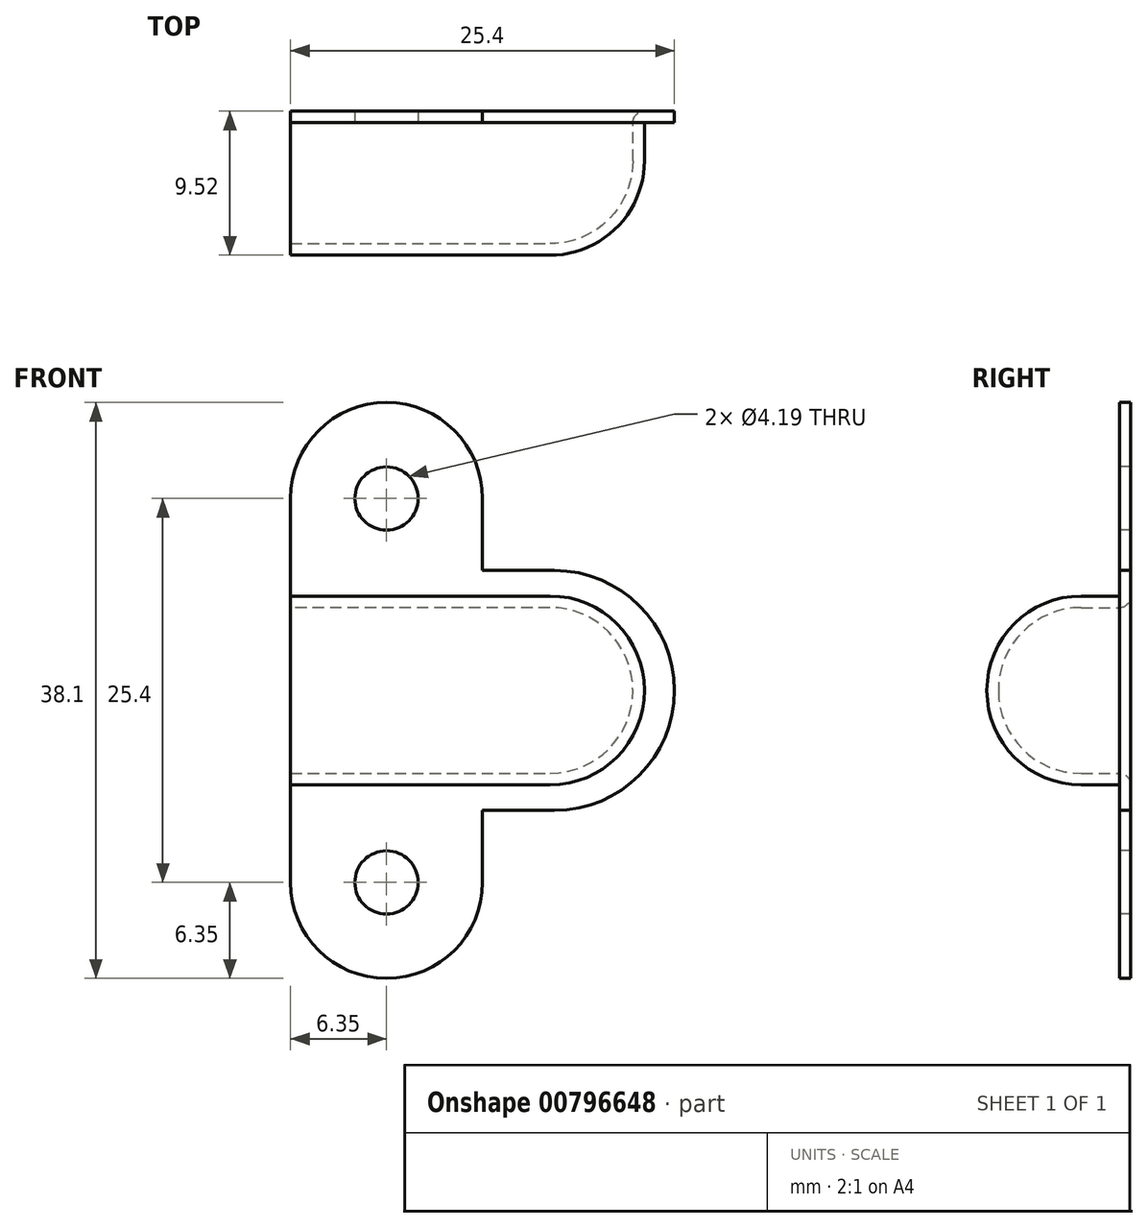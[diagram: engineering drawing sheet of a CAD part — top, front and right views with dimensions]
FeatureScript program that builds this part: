
annotation { "Feature Type Name" : "Feature", "Feature Type Description" : "" }
export const myFeature = defineFeature(function(context is Context, id is Id, definition is map)
    precondition{}
    {
        {
            var Q0;
            Q0=qCreatedBy(makeId("Front.planeOp"),FACE);
            var sketch = newSketch(context, id + "F0", { "sketchPlane" : qUnion([Q0])});
            skLineSegment(sketch, "E0.0.2", {"start": v(0, 12.7) * mm, "end": v(0, -12.7) * mm});
            skArc(sketch, "E0.0.3", {"start": v(0, -12.7) * mm, "mid": v(6.35, -19.05) * mm, "end": v(12.7, -12.7) * mm});
            skLineSegment(sketch, "E0.0.4", {"start": v(12.7, -12.7) * mm, "end": v(12.7, -7.94) * mm});
            skLineSegment(sketch, "E0.0.5", {"start": v(12.7, -7.94) * mm, "end": v(17.46, -7.94) * mm});
            skArc(sketch, "E0.0.6", {"start": v(17.46, -7.94) * mm, "mid": v(25.4, 0) * mm, "end": v(17.46, 7.94) * mm});
            skLineSegment(sketch, "E0.0.7", {"start": v(17.46, 7.94) * mm, "end": v(12.7, 7.94) * mm});
            skLineSegment(sketch, "E0.0.8", {"start": v(12.7, 7.94) * mm, "end": v(12.7, 12.7) * mm});
            skArc(sketch, "E0.0.9", {"start": v(12.7, 12.7) * mm, "mid": v(6.35, 19.05) * mm, "end": v(0, 12.7) * mm});
            skLineSegment(sketch, "E1", {"start": v(0, 0) * mm, "end": v(25.4, 0) * mm, "construction": true});
            skSolve(sketch);
        }
        {
            var Q0;
            Q0 = qSketchRegion(id + "F0", true);
            extrude(context, id + "F1", {"entities" : qUnion([Q0]), "oppositeDirection" : true, "depth" : 0.76 * mm, "offsetDistance" : 25.4 * mm});
        }
        {
            var Q0;
            Q0=makeQuery(id+"F1.opExtrude","CAP_FACE",FACE,{"disambiguationData":[OSD([sQuery(id+"F0.wireOp",EDGE,"E0.0.2"),sQuery(id+"F0.wireOp",EDGE,"E0.0.3"),sQuery(id+"F0.wireOp",EDGE,"E0.0.4"),sQuery(id+"F0.wireOp",EDGE,"E0.0.5"),sQuery(id+"F0.wireOp",EDGE,"E0.0.6"),sQuery(id+"F0.wireOp",EDGE,"E0.0.7"),sQuery(id+"F0.wireOp",EDGE,"E0.0.8"),sQuery(id+"F0.wireOp",EDGE,"E0.0.9")])],"isStart":true});
            var sketch = newSketch(context, id + "F2", { "sketchPlane" : qUnion([Q0])});
            skLineSegment(sketch, "E2.bottom", {"start": v(0, 6.25) * mm, "end": v(17.16, 6.25) * mm});
            skLineSegment(sketch, "E2.top", {"start": v(0, -6.25) * mm, "end": v(17.16, -6.25) * mm});
            skLineSegment(sketch, "E2.left", {"start": v(0, 6.25) * mm, "end": v(0, -6.25) * mm});
            skArc(sketch, "E3", {"start": v(17.16, -6.25) * mm, "mid": v(23.42, 0) * mm, "end": v(17.16, 6.25) * mm});
            skSolve(sketch);
        }
        {
            var Q0;
            Q0 = qSketchRegion(id + "F2", true);
            extrude(context, id + "F3", {"entities" : qUnion([Q0]), "operationType" : NewBodyOperationType.ADD, "depth" : 8.76 * mm, "offsetDistance" : 25.4 * mm});
        }
        {
            var Q0;
            Q0=makeQuery(id+"F3.opExtrude","CAP_EDGE",EDGE,{"disambiguationData":[OSD([sQuery(id+"F2.wireOp",EDGE,"E2.bottom")])],"isStart":false});
            fillet(context, id + "F4", {"entities" : qUnion([Q0]), "radius" : 6.25 * mm, "tangentPropagation" : true, "allowEdgeOverflow" : false});
        }
        {
            var Q0;
            Q0=makeQuery(id+"F1.opExtrude","CAP_FACE",FACE,{"disambiguationData":[OSD([sQuery(id+"F0.wireOp",EDGE,"E0.0.2"),sQuery(id+"F0.wireOp",EDGE,"E0.0.3"),sQuery(id+"F0.wireOp",EDGE,"E0.0.4"),sQuery(id+"F0.wireOp",EDGE,"E0.0.5"),sQuery(id+"F0.wireOp",EDGE,"E0.0.6"),sQuery(id+"F0.wireOp",EDGE,"E0.0.7"),sQuery(id+"F0.wireOp",EDGE,"E0.0.8"),sQuery(id+"F0.wireOp",EDGE,"E0.0.9")])],"isStart":true});
            var sketch = newSketch(context, id + "F5", { "sketchPlane" : qUnion([Q0])});
            skCircle(sketch, "E4", {"center": v(6.35, 12.7) * mm, "radius": 2.1 * mm});
            skCircle(sketch, "E5", {"center": v(6.35, -12.7) * mm, "radius": 2.1 * mm});
            skSolve(sketch);
        }
        {
            var Q0;
            Q0 = qSketchRegion(id + "F5", true);
            extrude(context, id + "F6", {"entities" : qUnion([Q0]), "operationType" : NewBodyOperationType.REMOVE, "endBound" : BoundingType.THROUGH_ALL, "oppositeDirection" : true, "depth" : 25.4 * mm, "offsetDistance" : 25.4 * mm});
        }
        {
            var Q0;
            Q0=makeQuery(id+"F3.boolean.opBoolean","MERGE",FACE,{"derivedFrom":[makeQuery(id+"F1.opExtrude","SWEPT_FACE",FACE,{"disambiguationData":[OSD([sQuery(id+"F0.wireOp",EDGE,"E0.0.2")])]}),makeQuery(id+"F3.opExtrude","SWEPT_FACE",FACE,{"disambiguationData":[OSD([sQuery(id+"F2.wireOp",EDGE,"E2.left")])]})]});
            shell(context, id + "F7", {"entities" : qUnion([Q0]), "thickness" : 0.76 * mm});
        }
        {
            var Q0;
            Q0=makeQuery(id+"F7.opShell","OFFSET_FACE",FACE,{"disambiguationData":[OSD([sQuery(id+"F0.wireOp",EDGE,"E0.0.2"),sQuery(id+"F0.wireOp",EDGE,"E0.0.3"),sQuery(id+"F0.wireOp",EDGE,"E0.0.4"),sQuery(id+"F0.wireOp",EDGE,"E0.0.5"),sQuery(id+"F0.wireOp",EDGE,"E0.0.6"),sQuery(id+"F0.wireOp",EDGE,"E0.0.7"),sQuery(id+"F0.wireOp",EDGE,"E0.0.8"),sQuery(id+"F0.wireOp",EDGE,"E0.0.9")])]});
            extrude(context, id + "F8", {"entities" : qUnion([Q0]), "operationType" : NewBodyOperationType.REMOVE, "endBound" : BoundingType.THROUGH_ALL, "oppositeDirection" : true, "depth" : 25.4 * mm, "offsetDistance" : 25.4 * mm});
        }
        {
            var Q0;
            Q0=makeQuery(id+"F3.opExtrude","CAP_EDGE",EDGE,{"disambiguationData":[OSD([sQuery(id+"F2.wireOp",EDGE,"E2.bottom")])],"isStart":true});
            var Q1;
            {var subQ0=sQuery(id+"F0.wireOp",EDGE,"E0.0.9");var subQ1=sQuery(id+"F0.wireOp",EDGE,"E0.0.8");var subQ2=sQuery(id+"F0.wireOp",EDGE,"E0.0.7");var subQ3=sQuery(id+"F0.wireOp",EDGE,"E0.0.6");var subQ4=sQuery(id+"F0.wireOp",EDGE,"E0.0.5");var subQ5=sQuery(id+"F0.wireOp",EDGE,"E0.0.4");var subQ6=sQuery(id+"F0.wireOp",EDGE,"E0.0.3");var subQ7=sQuery(id+"F0.wireOp",EDGE,"E0.0.2");Q1=makeQuery(id+"F8.boolean.opBoolean","INTERSECT",EDGE,{"derivedFrom":[makeQuery(id+"F1.opExtrude","CAP_FACE",FACE,{"disambiguationData":[OSD([subQ7,subQ6,subQ5,subQ4,subQ3,subQ2,subQ1,subQ0])],"isStart":false}),makeQuery(id+"F8.opExtrude","SWEPT_FACE",FACE,{"disambiguationData":[OSD([subQ7,subQ6,subQ5,subQ4,subQ3,subQ2,subQ1,subQ0,sQuery(id+"F2.wireOp",EDGE,"E2.bottom")])]})]});}
            fillet(context, id + "F9", {"entities" : qUnion([Q0, Q1]), "radius" : 0.76 * mm, "tangentPropagation" : true, "allowEdgeOverflow" : false});
        }
    });
